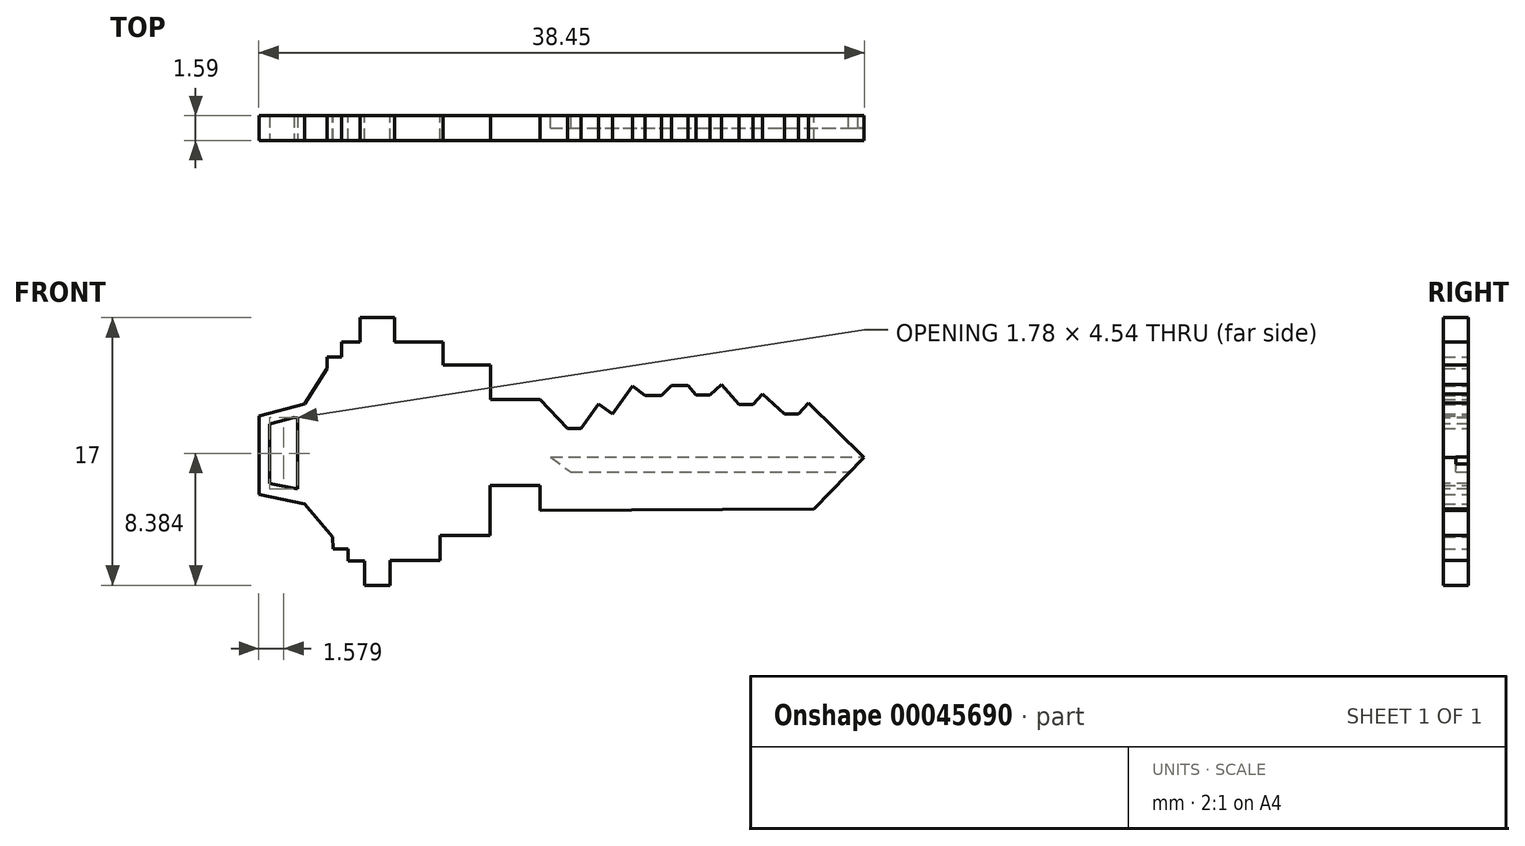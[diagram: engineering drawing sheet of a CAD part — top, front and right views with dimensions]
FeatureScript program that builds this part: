
annotation { "Feature Type Name" : "Feature", "Feature Type Description" : "" }
export const myFeature = defineFeature(function(context is Context, id is Id, definition is map)
    precondition{}
    {
        {
            var Q0;
            Q0=qCreatedBy(makeId("Front.planeOp"),FACE);
            var sketch = newSketch(context, id + "F0", { "sketchPlane" : qUnion([Q0])});
            skLineSegment(sketch, "E0", {"start": v(9.8, 21.76) * mm, "end": v(9.8, 23.35) * mm});
            skLineSegment(sketch, "E1", {"start": v(9.8, 23.35) * mm, "end": v(6.62, 23.35) * mm});
            skLineSegment(sketch, "E2", {"start": v(6.62, 23.35) * mm, "end": v(6.62, 20.17) * mm});
            skLineSegment(sketch, "E3", {"start": v(6.62, 20.17) * mm, "end": v(3.45, 20.17) * mm});
            skLineSegment(sketch, "E4", {"start": v(3.45, 20.17) * mm, "end": v(3.45, 18.59) * mm});
            skLineSegment(sketch, "E5", {"start": v(3.45, 18.59) * mm, "end": v(0.27, 18.59) * mm});
            skLineSegment(sketch, "E6", {"start": v(0.27, 18.59) * mm, "end": v(0.27, 17) * mm});
            skLineSegment(sketch, "E7", {"start": v(0.27, 17) * mm, "end": v(-1.38, 17) * mm});
            skLineSegment(sketch, "E8", {"start": v(-1.38, 17) * mm, "end": v(-1.38, 18.56) * mm});
            skLineSegment(sketch, "E9", {"start": v(-2.43, 18.56) * mm, "end": v(-1.38, 18.56) * mm});
            skLineSegment(sketch, "E10", {"start": v(-2.43, 19.32) * mm, "end": v(-2.43, 18.56) * mm});
            skLineSegment(sketch, "E11", {"start": v(-3.38, 19.32) * mm, "end": v(-2.43, 19.32) * mm});
            skLineSegment(sketch, "E12", {"start": v(-3.4, 20.06) * mm, "end": v(-3.38, 19.32) * mm});
            skLineSegment(sketch, "E13", {"start": v(-5.18, 22.17) * mm, "end": v(-3.4, 20.06) * mm});
            skLineSegment(sketch, "E14", {"start": v(-5.18, 22.17) * mm, "end": v(-5.18, 28.52) * mm});
            skLineSegment(sketch, "E15", {"start": v(-5.18, 28.52) * mm, "end": v(-3.74, 30.77) * mm});
            skLineSegment(sketch, "E16", {"start": v(-3.74, 30.77) * mm, "end": v(-3.74, 31.51) * mm});
            skLineSegment(sketch, "E17", {"start": v(-3.74, 31.51) * mm, "end": v(-2.81, 31.51) * mm});
            skLineSegment(sketch, "E18", {"start": v(-2.81, 31.51) * mm, "end": v(-2.81, 32.47) * mm});
            skLineSegment(sketch, "E19", {"start": v(-2.81, 32.47) * mm, "end": v(-1.64, 32.47) * mm});
            skLineSegment(sketch, "E20", {"start": v(-1.64, 32.47) * mm, "end": v(-1.64, 34) * mm});
            skLineSegment(sketch, "E21", {"start": v(-1.64, 34) * mm, "end": v(0.56, 34) * mm});
            skLineSegment(sketch, "E22", {"start": v(0.56, 34) * mm, "end": v(0.56, 32.47) * mm});
            skLineSegment(sketch, "E23", {"start": v(0.56, 32.47) * mm, "end": v(3.63, 32.47) * mm});
            skLineSegment(sketch, "E24", {"start": v(3.63, 32.47) * mm, "end": v(3.63, 31) * mm});
            skLineSegment(sketch, "E25", {"start": v(3.63, 31) * mm, "end": v(6.63, 31) * mm});
            skLineSegment(sketch, "E26", {"start": v(6.63, 31) * mm, "end": v(6.63, 28.8) * mm});
            skLineSegment(sketch, "E27", {"start": v(6.63, 28.8) * mm, "end": v(9.78, 28.8) * mm});
            skLineSegment(sketch, "E28", {"start": v(9.78, 28.8) * mm, "end": v(11.51, 26.98) * mm});
            skLineSegment(sketch, "E29", {"start": v(11.51, 26.98) * mm, "end": v(12.4, 26.98) * mm});
            skLineSegment(sketch, "E30", {"start": v(12.4, 26.98) * mm, "end": v(13.5, 28.51) * mm});
            skLineSegment(sketch, "E31", {"start": v(13.5, 28.51) * mm, "end": v(14.38, 27.88) * mm});
            skLineSegment(sketch, "E32", {"start": v(14.38, 27.88) * mm, "end": v(15.65, 29.65) * mm});
            skLineSegment(sketch, "E33", {"start": v(15.65, 29.65) * mm, "end": v(16.44, 29.08) * mm});
            skLineSegment(sketch, "E34", {"start": v(16.44, 29.08) * mm, "end": v(17.48, 29.08) * mm});
            skLineSegment(sketch, "E35", {"start": v(17.48, 29.08) * mm, "end": v(18.14, 29.68) * mm});
            skLineSegment(sketch, "E36", {"start": v(18.14, 29.68) * mm, "end": v(19.18, 29.68) * mm});
            skLineSegment(sketch, "E37", {"start": v(19.18, 29.68) * mm, "end": v(19.7, 29.1) * mm});
            skLineSegment(sketch, "E38", {"start": v(19.7, 29.1) * mm, "end": v(20.58, 29.1) * mm});
            skLineSegment(sketch, "E39", {"start": v(20.58, 29.1) * mm, "end": v(21.31, 29.75) * mm});
            skLineSegment(sketch, "E40", {"start": v(21.31, 29.75) * mm, "end": v(22.43, 28.5) * mm});
            skLineSegment(sketch, "E41", {"start": v(22.43, 28.5) * mm, "end": v(23.3, 28.5) * mm});
            skLineSegment(sketch, "E42", {"start": v(23.3, 28.5) * mm, "end": v(23.9, 29.17) * mm});
            skLineSegment(sketch, "E43", {"start": v(23.9, 29.17) * mm, "end": v(25.32, 27.9) * mm});
            skLineSegment(sketch, "E44", {"start": v(25.32, 27.9) * mm, "end": v(26.18, 27.9) * mm});
            skLineSegment(sketch, "E45", {"start": v(26.18, 27.9) * mm, "end": v(26.84, 28.58) * mm});
            skLineSegment(sketch, "E46", {"start": v(26.84, 28.58) * mm, "end": v(30.37, 25.12) * mm});
            skLineSegment(sketch, "E47", {"start": v(30.37, 25.12) * mm, "end": v(27.18, 21.87) * mm});
            skLineSegment(sketch, "E48", {"start": v(27.18, 21.87) * mm, "end": v(9.8, 21.76) * mm});
            skLineSegment(sketch, "E49", {"start": v(-5.18, 28.52) * mm, "end": v(-8.08, 27.77) * mm});
            skLineSegment(sketch, "E50", {"start": v(-5.18, 22.17) * mm, "end": v(-8.08, 22.76) * mm});
            skLineSegment(sketch, "E51", {"start": v(-8.08, 22.76) * mm, "end": v(-8.08, 27.15) * mm});
            skLineSegment(sketch, "E52", {"start": v(-8.08, 27.15) * mm, "end": v(-8.08, 27.77) * mm});
            skSolve(sketch);
        }
        {
            var Q0;
            Q0=makeQuery(id+"F0.imprint","IMPRINT",FACE,{"disambiguationData":[TD([[makeQuery(id+"F0.imprint","IMPRINT",EDGE,{"derivedFrom":sQuery(id+"F0.wireOp",EDGE,"E0")}),-1.0]])]});
            var sketch = newSketch(context, id + "F1", { "sketchPlane" : qUnion([Q0])});
            skLineSegment(sketch, "E53", {"start": v(28.02, 25.14) * mm, "end": v(10.45, 25.14) * mm});
            skLineSegment(sketch, "E54", {"start": v(10.45, 25.14) * mm, "end": v(11.74, 24.2) * mm});
            skLineSegment(sketch, "E55", {"start": v(11.74, 24.2) * mm, "end": v(29.37, 24.2) * mm});
            skLineSegment(sketch, "E56", {"start": v(28.02, 25.14) * mm, "end": v(30.48, 25.14) * mm});
            skLineSegment(sketch, "E57", {"start": v(29.37, 24.2) * mm, "end": v(30.48, 25.14) * mm});
            skSolve(sketch);
        }
        {
            var Q0;
            Q0 = qSketchRegion(id + "F0", true);
            extrude(context, id + "F2", {"entities" : qUnion([Q0]), "depth" : 1.59 * mm});
        }
        {
            var Q0;
            Q0=makeQuery(id+"F2.opExtrude","CAP_FACE",FACE,{"disambiguationData":[OSD([sQuery(id+"F0.wireOp",EDGE,"E0"),sQuery(id+"F0.wireOp",EDGE,"E1"),sQuery(id+"F0.wireOp",EDGE,"E2"),sQuery(id+"F0.wireOp",EDGE,"E3"),sQuery(id+"F0.wireOp",EDGE,"E4"),sQuery(id+"F0.wireOp",EDGE,"E5"),sQuery(id+"F0.wireOp",EDGE,"E6"),sQuery(id+"F0.wireOp",EDGE,"E7"),sQuery(id+"F0.wireOp",EDGE,"E8"),sQuery(id+"F0.wireOp",EDGE,"E9"),sQuery(id+"F0.wireOp",EDGE,"E10"),sQuery(id+"F0.wireOp",EDGE,"E11"),sQuery(id+"F0.wireOp",EDGE,"E12"),sQuery(id+"F0.wireOp",EDGE,"E13"),sQuery(id+"F0.wireOp",EDGE,"E15"),sQuery(id+"F0.wireOp",EDGE,"E16"),sQuery(id+"F0.wireOp",EDGE,"E17"),sQuery(id+"F0.wireOp",EDGE,"E18"),sQuery(id+"F0.wireOp",EDGE,"E19"),sQuery(id+"F0.wireOp",EDGE,"E20"),sQuery(id+"F0.wireOp",EDGE,"E21"),sQuery(id+"F0.wireOp",EDGE,"E22"),sQuery(id+"F0.wireOp",EDGE,"E23"),sQuery(id+"F0.wireOp",EDGE,"E24"),sQuery(id+"F0.wireOp",EDGE,"E25"),sQuery(id+"F0.wireOp",EDGE,"E26"),sQuery(id+"F0.wireOp",EDGE,"E27"),sQuery(id+"F0.wireOp",EDGE,"E28"),sQuery(id+"F0.wireOp",EDGE,"E29"),sQuery(id+"F0.wireOp",EDGE,"E30"),sQuery(id+"F0.wireOp",EDGE,"E31"),sQuery(id+"F0.wireOp",EDGE,"E32"),sQuery(id+"F0.wireOp",EDGE,"E33"),sQuery(id+"F0.wireOp",EDGE,"E34"),sQuery(id+"F0.wireOp",EDGE,"E35"),sQuery(id+"F0.wireOp",EDGE,"E36"),sQuery(id+"F0.wireOp",EDGE,"E37"),sQuery(id+"F0.wireOp",EDGE,"E38"),sQuery(id+"F0.wireOp",EDGE,"E39"),sQuery(id+"F0.wireOp",EDGE,"E40"),sQuery(id+"F0.wireOp",EDGE,"E41"),sQuery(id+"F0.wireOp",EDGE,"E42"),sQuery(id+"F0.wireOp",EDGE,"E43"),sQuery(id+"F0.wireOp",EDGE,"E44"),sQuery(id+"F0.wireOp",EDGE,"E45"),sQuery(id+"F0.wireOp",EDGE,"E46"),sQuery(id+"F0.wireOp",EDGE,"E47"),sQuery(id+"F0.wireOp",EDGE,"E48"),sQuery(id+"F0.wireOp",EDGE,"E49"),sQuery(id+"F0.wireOp",EDGE,"E50"),sQuery(id+"F0.wireOp",EDGE,"E51"),sQuery(id+"F0.wireOp",EDGE,"E52")])],"isStart":false});
            var sketch = newSketch(context, id + "F3", { "sketchPlane" : qUnion([Q0])});
            skLineSegment(sketch, "E58", {"start": v(-5.83, 27.65) * mm, "end": v(-7.4, 27.25) * mm});
            skLineSegment(sketch, "E59", {"start": v(-7.4, 27.25) * mm, "end": v(-7.4, 23.46) * mm});
            skLineSegment(sketch, "E60", {"start": v(-7.4, 23.46) * mm, "end": v(-5.6, 23.12) * mm});
            skLineSegment(sketch, "E61", {"start": v(-5.6, 23.12) * mm, "end": v(-5.6, 27.65) * mm});
            skLineSegment(sketch, "E62", {"start": v(-5.6, 27.65) * mm, "end": v(-5.83, 27.65) * mm});
            skSolve(sketch);
        }
        {
            var Q0;
            Q0=makeQuery(id+"F3.imprint","IMPRINT",FACE,{"disambiguationData":[TD([[makeQuery(id+"F3.imprint","IMPRINT",EDGE,{"derivedFrom":sQuery(id+"F3.wireOp",EDGE,"E58")}),1.0]])]});
            extrude(context, id + "F4", {"entities" : qUnion([Q0]), "operationType" : NewBodyOperationType.REMOVE, "oppositeDirection" : true, "depth" : 1.59 * mm});
        }
        {
            var Q0;
            Q0 = qSketchRegion(id + "F1", true);
            extrude(context, id + "F5", {"entities" : qUnion([Q0]), "operationType" : NewBodyOperationType.REMOVE, "depth" : 0.8 * mm});
        }
    });
